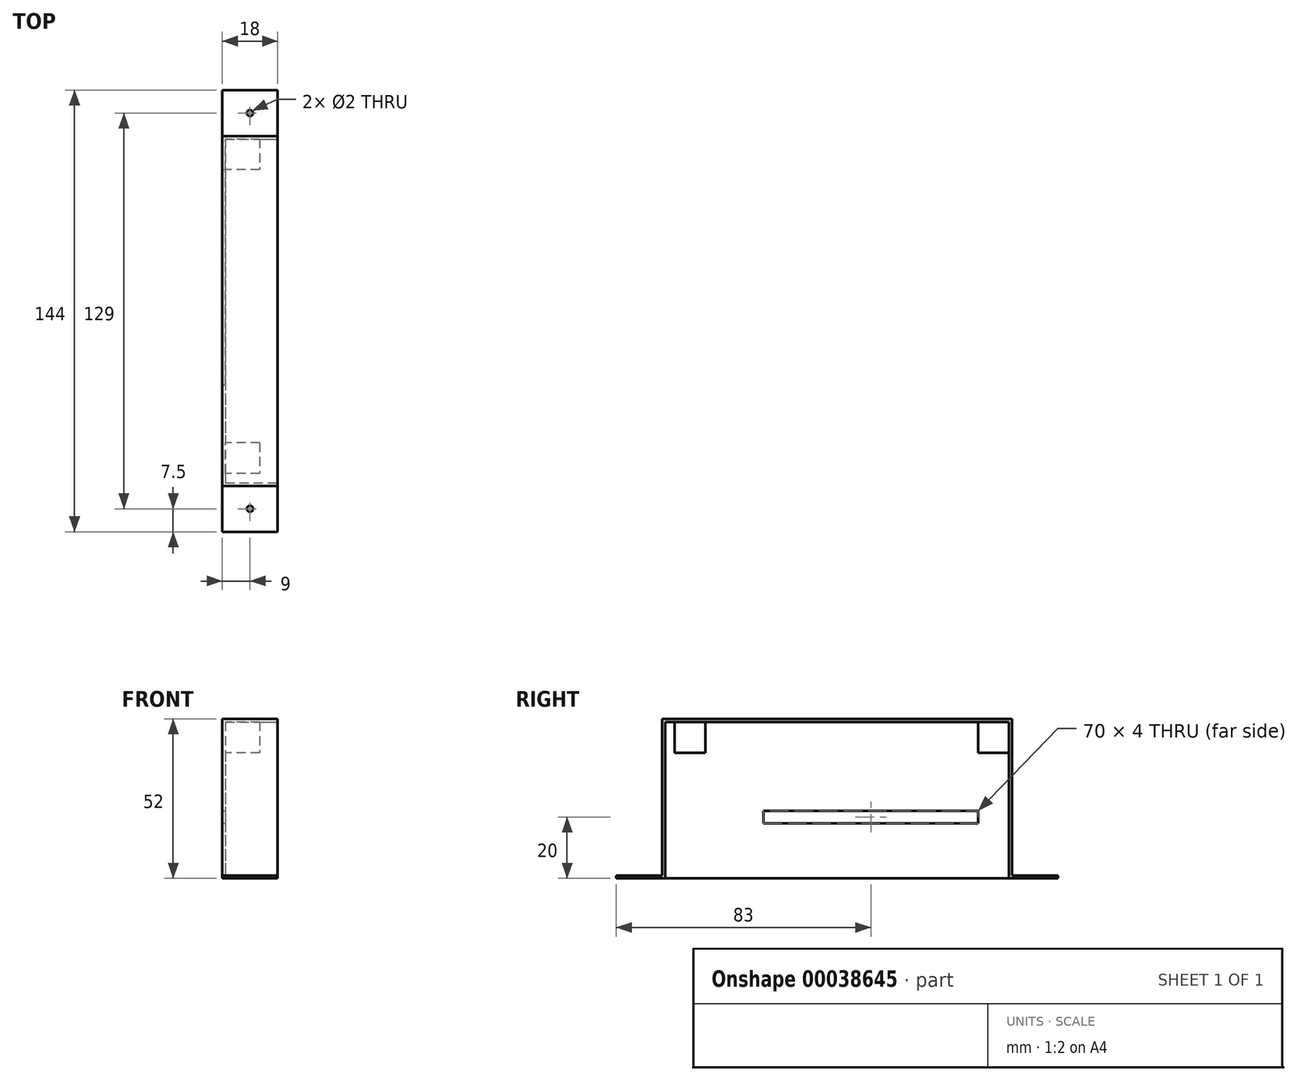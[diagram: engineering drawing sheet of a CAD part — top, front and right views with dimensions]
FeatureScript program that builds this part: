
annotation { "Feature Type Name" : "Feature", "Feature Type Description" : "" }
export const myFeature = defineFeature(function(context is Context, id is Id, definition is map)
    precondition{}
    {
        {
            var Q0;
            Q0=qCreatedBy(makeId("Top.planeOp"),FACE);
            var sketch = newSketch(context, id + "F0", { "sketchPlane" : qUnion([Q0])});
            skLineSegment(sketch, "E0.bottom", {"start": v(-18, 57) * mm, "end": v(0, 57) * mm});
            skLineSegment(sketch, "E0.top", {"start": v(-18, -57) * mm, "end": v(0, -57) * mm});
            skLineSegment(sketch, "E0.left", {"start": v(-18, 57) * mm, "end": v(-18, -57) * mm});
            skLineSegment(sketch, "E0.right", {"start": v(0, 57) * mm, "end": v(0, -57) * mm});
            skSolve(sketch);
        }
        {
            var Q0;
            Q0=qSketchRegion(id+"F0",true);
            extrude(context, id + "F1", {"entities" : qUnion([Q0]), "depth" : 52 * mm});
        }
        {
            var Q0;
            Q0=makeQuery(id+"F1.opExtrude","CAP_FACE",FACE,{"disambiguationData":[OSD([sQuery(id+"F0.wireOp",EDGE,"E0.bottom"),sQuery(id+"F0.wireOp",EDGE,"E0.top"),sQuery(id+"F0.wireOp",EDGE,"E0.left"),sQuery(id+"F0.wireOp",EDGE,"E0.right")])],"isStart":true});
            var sketch = newSketch(context, id + "F2", { "sketchPlane" : qUnion([Q0])});
            skLineSegment(sketch, "E1.bottom", {"start": v(-17, -56) * mm, "end": v(0, -56) * mm});
            skLineSegment(sketch, "E1.top", {"start": v(-17, 56) * mm, "end": v(0, 56) * mm});
            skLineSegment(sketch, "E1.left", {"start": v(-17, -56) * mm, "end": v(-17, 56) * mm});
            skLineSegment(sketch, "E1.right", {"start": v(0, -56) * mm, "end": v(0, 56) * mm});
            skSolve(sketch);
        }
        {
            var Q0;
            Q0=qSketchRegion(id+"F2",true);
            extrude(context, id + "F3", {"entities" : qUnion([Q0]), "operationType" : NewBodyOperationType.REMOVE, "oppositeDirection" : true, "depth" : 51 * mm});
        }
        {
            var Q0;
            Q0=qCreatedBy(makeId("Top.planeOp"),FACE);
            var sketch = newSketch(context, id + "F4", { "sketchPlane" : qUnion([Q0])});
            skLineSegment(sketch, "E2.bottom", {"start": v(0, 57) * mm, "end": v(-18, 57) * mm});
            skLineSegment(sketch, "E2.top", {"start": v(0, 72) * mm, "end": v(-18, 72) * mm});
            skLineSegment(sketch, "E2.left", {"start": v(0, 57) * mm, "end": v(0, 72) * mm});
            skLineSegment(sketch, "E2.right", {"start": v(-18, 57) * mm, "end": v(-18, 72) * mm});
            skLineSegment(sketch, "E3.bottom", {"start": v(-18, -72) * mm, "end": v(0, -72) * mm});
            skLineSegment(sketch, "E3.top", {"start": v(-18, -57) * mm, "end": v(0, -57) * mm});
            skLineSegment(sketch, "E3.left", {"start": v(-18, -72) * mm, "end": v(-18, -57) * mm});
            skLineSegment(sketch, "E3.right", {"start": v(0, -72) * mm, "end": v(0, -57) * mm});
            skCircle(sketch, "E4", {"center": v(-9, -64.5) * mm, "radius": 1 * mm});
            skCircle(sketch, "E5", {"center": v(-9, 64.5) * mm, "radius": 1 * mm});
            skLineSegment(sketch, "E6", {"start": v(-9, -72) * mm, "end": v(-9, -57) * mm, "construction": true});
            skLineSegment(sketch, "E7", {"start": v(-18, -64.5) * mm, "end": v(-9, -64.5) * mm, "construction": true});
            skLineSegment(sketch, "E8", {"start": v(-9, -64.5) * mm, "end": v(0, -64.5) * mm, "construction": true});
            skLineSegment(sketch, "E9", {"start": v(-9, 57) * mm, "end": v(-9, 72) * mm, "construction": true});
            skLineSegment(sketch, "E10", {"start": v(-18, 64.5) * mm, "end": v(-9, 64.5) * mm, "construction": true});
            skLineSegment(sketch, "E11", {"start": v(-9, 64.5) * mm, "end": v(0, 64.5) * mm, "construction": true});
            skSolve(sketch);
        }
        {
            var Q0;
            Q0=qSketchRegion(id+"F4",true);
            extrude(context, id + "F5", {"entities" : qUnion([Q0]), "operationType" : NewBodyOperationType.ADD, "depth" : 1 * mm});
        }
        {
            var Q0;
            Q0=makeQuery(id+"F3.boolean.opBoolean","COPY",FACE,{"derivedFrom":makeQuery(id+"F3.opExtrude","SWEPT_FACE",FACE,{"disambiguationData":[OSD([sQuery(id+"F2.wireOp",EDGE,"E1.left")])]})});
            var sketch = newSketch(context, id + "F6", { "sketchPlane" : qUnion([Q0])});
            skLineSegment(sketch, "E12.bottom", {"start": v(-24, 22) * mm, "end": v(46, 22) * mm});
            skLineSegment(sketch, "E12.top", {"start": v(-24, 18) * mm, "end": v(46, 18) * mm});
            skLineSegment(sketch, "E12.left", {"start": v(-24, 22) * mm, "end": v(-24, 18) * mm});
            skLineSegment(sketch, "E12.right", {"start": v(46, 22) * mm, "end": v(46, 18) * mm});
            skSolve(sketch);
        }
        {
            var Q0;
            Q0=qSketchRegion(id+"F6",true);
            extrude(context, id + "F7", {"entities" : qUnion([Q0]), "operationType" : NewBodyOperationType.REMOVE, "oppositeDirection" : true, "depth" : 1 * mm});
        }
        {
            var Q0;
            Q0=makeQuery(id+"F3.boolean.opBoolean","COPY",FACE,{"derivedFrom":makeQuery(id+"F3.opExtrude","SWEPT_FACE",FACE,{"disambiguationData":[OSD([sQuery(id+"F2.wireOp",EDGE,"E1.left")])]})});
            var sketch = newSketch(context, id + "F8", { "sketchPlane" : qUnion([Q0])});
            skLineSegment(sketch, "E13", {"start": v(-56, 41) * mm, "end": v(56, 41) * mm, "construction": true});
            skLineSegment(sketch, "E14.bottom", {"start": v(-53, 51) * mm, "end": v(-43, 51) * mm});
            skLineSegment(sketch, "E14.top", {"start": v(-53, 41) * mm, "end": v(-43, 41) * mm});
            skLineSegment(sketch, "E14.left", {"start": v(-53, 51) * mm, "end": v(-53, 41) * mm});
            skLineSegment(sketch, "E14.right", {"start": v(-43, 51) * mm, "end": v(-43, 41) * mm});
            skLineSegment(sketch, "E15.bottom", {"start": v(46, 51) * mm, "end": v(56, 51) * mm});
            skLineSegment(sketch, "E15.top", {"start": v(46, 41) * mm, "end": v(56, 41) * mm});
            skLineSegment(sketch, "E15.left", {"start": v(46, 51) * mm, "end": v(46, 41) * mm});
            skLineSegment(sketch, "E15.right", {"start": v(56, 51) * mm, "end": v(56, 41) * mm});
            skSolve(sketch);
        }
        {
            var Q0;
            Q0 = qSketchRegion(id + "F8", true);
            extrude(context, id + "F9", {"entities" : qUnion([Q0]), "operationType" : NewBodyOperationType.ADD, "depth" : 11.2 * mm});
        }
    });
